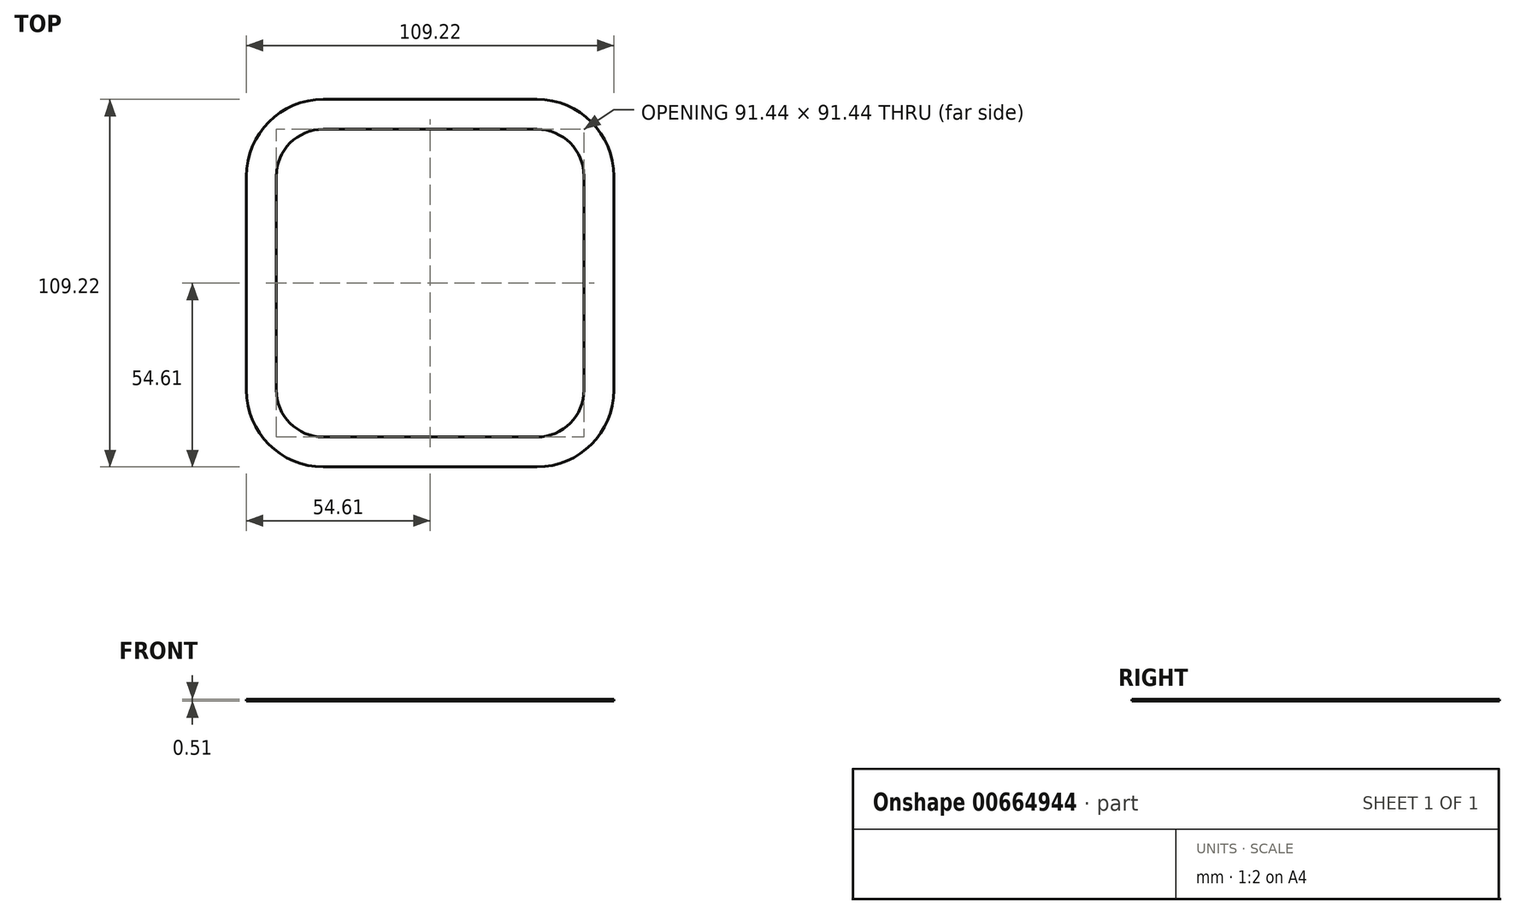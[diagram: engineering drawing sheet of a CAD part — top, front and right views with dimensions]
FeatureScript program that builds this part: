
annotation { "Feature Type Name" : "Feature", "Feature Type Description" : "" }
export const myFeature = defineFeature(function(context is Context, id is Id, definition is map)
    precondition{}
    {
        {
            var Q0;
            Q0=qCreatedBy(makeId("Top.planeOp"),FACE);
            var sketch = newSketch(context, id + "F0", { "sketchPlane" : qUnion([Q0])});
            skLineSegment(sketch, "E0.bottom", {"start": v(31.75, 54.61) * mm, "end": v(-31.75, 54.61) * mm});
            skLineSegment(sketch, "E0.top", {"start": v(31.75, -54.61) * mm, "end": v(-31.75, -54.61) * mm});
            skLineSegment(sketch, "E0.left", {"start": v(54.61, 31.75) * mm, "end": v(54.61, -31.75) * mm});
            skLineSegment(sketch, "E0.right", {"start": v(-54.61, 31.75) * mm, "end": v(-54.61, -31.75) * mm});
            skPoint(sketch, "E0.middle", {"position": v(0, 0) * mm});
            skPoint(sketch, "E1.visualSharp", {"position": v(-54.61, 54.61) * mm});
            skArc(sketch, "E1.filletArc", {"start": v(-31.75, 54.61) * mm, "mid": v(-47.91, 47.91) * mm, "end": v(-54.61, 31.75) * mm});
            skPoint(sketch, "E2.visualSharp", {"position": v(54.61, 54.61) * mm});
            skArc(sketch, "E2.filletArc", {"start": v(54.61, 31.75) * mm, "mid": v(47.91, 47.91) * mm, "end": v(31.75, 54.61) * mm});
            skPoint(sketch, "E3.visualSharp", {"position": v(54.61, -54.61) * mm});
            skArc(sketch, "E3.filletArc", {"start": v(31.75, -54.61) * mm, "mid": v(47.91, -47.91) * mm, "end": v(54.61, -31.75) * mm});
            skPoint(sketch, "E4.visualSharp", {"position": v(-54.61, -54.61) * mm});
            skArc(sketch, "E4.filletArc", {"start": v(-54.61, -31.75) * mm, "mid": v(-47.91, -47.91) * mm, "end": v(-31.75, -54.61) * mm});
            skLineSegment(sketch, "E5.bottom", {"start": v(31.75, -45.72) * mm, "end": v(-31.75, -45.72) * mm});
            skLineSegment(sketch, "E5.top", {"start": v(31.75, 45.72) * mm, "end": v(-31.75, 45.72) * mm});
            skLineSegment(sketch, "E5.left", {"start": v(45.72, -31.75) * mm, "end": v(45.72, 31.75) * mm});
            skLineSegment(sketch, "E5.right", {"start": v(-45.72, -31.75) * mm, "end": v(-45.72, 31.75) * mm});
            skPoint(sketch, "E6.visualSharp", {"position": v(-45.72, 45.72) * mm});
            skArc(sketch, "E6.filletArc", {"start": v(-31.75, 45.72) * mm, "mid": v(-41.63, 41.63) * mm, "end": v(-45.72, 31.75) * mm});
            skPoint(sketch, "E7.visualSharp", {"position": v(-45.72, -45.72) * mm});
            skArc(sketch, "E7.filletArc", {"start": v(-45.72, -31.75) * mm, "mid": v(-41.63, -41.63) * mm, "end": v(-31.75, -45.72) * mm});
            skPoint(sketch, "E8.visualSharp", {"position": v(45.72, -45.72) * mm});
            skArc(sketch, "E8.filletArc", {"start": v(31.75, -45.72) * mm, "mid": v(41.63, -41.63) * mm, "end": v(45.72, -31.75) * mm});
            skPoint(sketch, "E9.visualSharp", {"position": v(45.72, 45.72) * mm});
            skArc(sketch, "E9.filletArc", {"start": v(45.72, 31.75) * mm, "mid": v(41.63, 41.63) * mm, "end": v(31.75, 45.72) * mm});
            skSolve(sketch);
        }
        {
            var Q0;
            Q0 = qSketchRegion(id + "F0", true);
            extrude(context, id + "F1", {"entities" : qUnion([Q0]), "depth" : 0.5 * mm, "offsetDistance" : 25.4 * mm});
        }
    });
